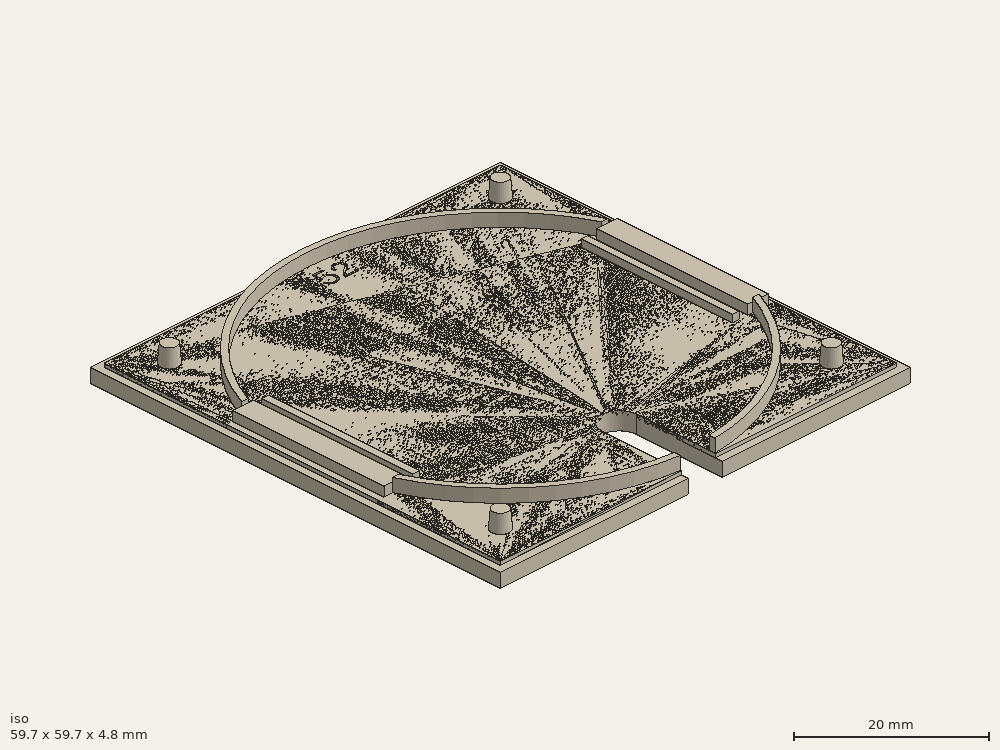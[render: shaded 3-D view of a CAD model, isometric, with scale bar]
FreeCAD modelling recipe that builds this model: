
FCSTD DOCUMENT  (FreeCAD 0.16R)
Label: edizio_part_752_cable-slot
License: All rights reserved
LicenseURL: http://en.wikipedia.org/wiki/All_rights_reserved
objects: Part::Box×25, Part::Cut×9, Part::Cone×4, Part::Cylinder×3, Part::Fuse×2, Part::Part2DObjectPython×1, Part::Extrusion×1, Part::FeaturePython×1
note: 46 computed .brp shape members not serialized (recipe doc carries the construction recipe); baked Part::Feature solids carry a one-line shape summary decoded from their .brp

FEATURE [Part::Box] Box  label="Front"
  Height = 1.9
  Length = 59.7
  Width = 59.7
FEATURE [Part::Box] Box001  label="Layer_Inside_Base"
  Height = 0.5
  Length = 57.7
  Placement = pos=(1,1,1.9) rot=(0,0,1;0rad)
  Width = 57.7
FEATURE [Part::Cylinder] Cylinder  label="Cylinder_Outside"
  Angle = 360
  Height = 1.8
  Placement = pos=(29.85,29.85,2.4) rot=(0,0,1;0rad)
  Radius = 28.85
FEATURE [Part::Cylinder] Cylinder001  label="Cylinder_Inside"
  Angle = 360
  Height = 1.8
  Placement = pos=(29.85,29.85,2.4) rot=(0,0,1;0rad)
  Radius = 28
FEATURE [Part::Cut] Cut  label="Cylinder_Base"
  Base = -> Cylinder
  Tool = -> Cylinder001
FEATURE [Part::Cone] Cone  label="Cone_001"
  Angle = 360
  Height = 2.4
  Placement = pos=(5.8,5.8,2.4) rot=(0,0,1;0rad)
  Radius1 = 1.25
  Radius2 = 1.05
FEATURE [Part::Cone] Cone001  label="Cone_002"
  Angle = 360
  Height = 2.4
  Placement = pos=(54,5.8,2.4) rot=(0,0,1;0rad)
  Radius1 = 1.25
  Radius2 = 1.05
FEATURE [Part::Cone] Cone002  label="Cone_003"
  Angle = 360
  Height = 2.4
  Placement = pos=(54,54,2.4) rot=(0,0,1;0rad)
  Radius1 = 1.25
  Radius2 = 1.05
FEATURE [Part::Cone] Cone003  label="Cone_004"
  Angle = 360
  Height = 2.4
  Placement = pos=(5.8,54,2.4) rot=(0,0,1;0rad)
  Radius1 = 1.25
  Radius2 = 1.05
FEATURE [Part::Box] Box002  label="Cut_001"
  Height = 2.5
  Length = 5
  Placement = pos=(0,18.85,1.9) rot=(0,0,1;0rad)
  Width = 22
FEATURE [Part::Box] Box003  label="Cut_002"
  Height = 2.5
  Length = 5
  Placement = pos=(54.7,18.85,1.9) rot=(0,0,1;0rad)
  Width = 22
FEATURE [Part::Cut] Cut001  label="Cylinder_Cut001"
  Base = -> Cut
  Tool = -> Box002
FEATURE [Part::Cut] Cut002  label="Cylinder"
  Base = -> Cut001
  Tool = -> Box003
FEATURE [Part::Box] Box004  label="Cut_003"
  Height = 1.9
  Length = 5
  Placement = pos=(0,18.85,1.9) rot=(0,0,1;0rad)
  Width = 22
FEATURE [Part::Box] Box005  label="Cut_004"
  Height = 1.9
  Length = 5
  Placement = pos=(54.7,18.85,1.9) rot=(0,0,1;0rad)
  Width = 22
FEATURE [Part::Cut] Cut003  label="Layer_Inside_Cut003"
  Base = -> Box001
  Tool = -> Box004
FEATURE [Part::Cut] Cut004  label="Layer_Inside"
  Base = -> Cut003
  Tool = -> Box005
FEATURE [Part::Box] Box006  label="Cube_001"
  Height = 0.1
  Length = 1
  Placement = pos=(1.9,21,1.9) rot=(0,0,1;0rad)
  Width = 1
FEATURE [Part::Box] Box007  label="Cube_002"
  Height = 0.1
  Length = 1
  Placement = pos=(1.9,27.7,1.9) rot=(0,0,1;0rad)
  Width = 1
FEATURE [Part::Box] Box008  label="Cube_003"
  Height = 0.1
  Length = 1
  Placement = pos=(1.9,30.9,1.9) rot=(0,0,1;0rad)
  Width = 1
FEATURE [Part::Box] Box009  label="Cube_004"
  Height = 0.1
  Length = 1
  Placement = pos=(1.9,37.7,1.9) rot=(0,0,1;0rad)
  Width = 1
FEATURE [Part::Box] Box010  label="Cube_005"
  Height = 0.1
  Length = 1
  Placement = pos=(56.8,21,1.9) rot=(0,0,1;0rad)
  Width = 1
FEATURE [Part::Box] Box011  label="Cube_006"
  Height = 0.1
  Length = 1
  Placement = pos=(56.8,27.7,1.9) rot=(0,0,1;0rad)
  Width = 1
FEATURE [Part::Box] Box012  label="Cube_007"
  Height = 0.1
  Length = 1
  Placement = pos=(56.8,30.9,1.9) rot=(0,0,1;0rad)
  Width = 1
FEATURE [Part::Box] Box013  label="Cube_008"
  Height = 0.1
  Length = 1
  Placement = pos=(56.8,37.7,1.9) rot=(0,0,1;0rad)
  Width = 1
FEATURE [Part::Box] Box014  label="Cube_011"
  Height = 0.4
  Length = 3
  Placement = pos=(1.9,18.85,1.9) rot=(0,0,1;0rad)
  Width = 1.3
FEATURE [Part::Box] Box015  label="Cube_012"
  Height = 0.4
  Length = 3
  Placement = pos=(54.9,18.85,1.9) rot=(0,0,1;0rad)
  Width = 1.3
FEATURE [Part::Box] Box016  label="Cube_013"
  Height = 0.4
  Length = 3
  Placement = pos=(1.9,39.55,1.9) rot=(0,0,1;0rad)
  Width = 1.3
FEATURE [Part::Box] Box017  label="Cube_014"
  Height = 0.4
  Length = 3
  Placement = pos=(54.9,39.55,1.9) rot=(0,0,1;0rad)
  Width = 1.3
FEATURE [Part::Box] Box018  label="Cube_015"
  Height = 0.4
  Length = 3
  Placement = pos=(1.9,29.35,1.9) rot=(0,0,1;0rad)
  Width = 1
FEATURE [Part::Box] Box019  label="Cube_016"
  Height = 0.4
  Length = 3
  Placement = pos=(54.9,29.35,1.9) rot=(0,0,1;0rad)
  Width = 1
FEATURE [Part::Box] Box020  label="Cube_021"
  Height = 1.4
  Length = 3
  Placement = pos=(1.9,18.85,2.3) rot=(0,0,1;0rad)
  Width = 22
FEATURE [Part::Box] Box021  label="Cube_022"
  Height = 1.4
  Length = 3
  Placement = pos=(54.86,18.85,2.3) rot=(0,0,1;0rad)
  Width = 22
FEATURE [Part::Box] Box022  label="Cube_031"
  Height = 1
  Length = 1
  Placement = pos=(6.1,18.85,2.4) rot=(0,0,1;0rad)
  Width = 22
FEATURE [Part::Box] Box023  label="Cube_032"
  Height = 1
  Length = 1
  Placement = pos=(52.6,18.85,2.4) rot=(0,0,1;0rad)
  Width = 22
FEATURE [Part::Part2DObjectPython] ShapeString  # Draft 2D object (typed FeaturePython)
  FontFile = <path>
  Size = 0.1
  String = 752
  Tracking = 0
FEATURE [Part::Extrusion] Extrude001
  Base = -> ShapeString
  Dir = (0,0,0.1)
  Placement = pos=(0,0,1.9) rot=(0,0,1;0rad)
  Solid = true
FEATURE [Part::FeaturePython] Scale  # Draft clone (typed FeaturePython)
  Objects = -> [Extrude001]
  Placement = pos=(25.9,53.5,4.4) rot=(0,0,1;0rad)
  Scale = (22,22,0)
FEATURE [Part::Cylinder] Cylinder002  label="Cylinder001"
  Angle = 360
  Height = 5
  Placement = pos=(29.85,12.5,0) rot=(0,0,1;0rad)
  Radius = 2.5
FEATURE [Part::Box] Box024  label="Cube"
  Height = 5
  Length = 5
  Placement = pos=(27.35,0,0) rot=(0,0,1;0rad)
  Width = 12.5
FEATURE [Part::Fuse] Fusion  label="Plate"
  Base = -> Box
  Tool = -> Box001
FEATURE [Part::Fuse] Fusion001  label="Plate_and_Ring"
  Base = -> Cut002
  Tool = -> Fusion
FEATURE [Part::Cut] Cut005
  Base = -> Fusion001
  Tool = -> Box024
FEATURE [Part::Cut] Cut006
  Base = -> Cut005
  Tool = -> Cylinder002
FEATURE [Part::Cut] Cut007
  Base = -> Cut004
  Tool = -> Cylinder002
FEATURE [Part::Cut] Cut008
  Base = -> Cut007
  Tool = -> Box024
note: 1 file-system path scrubbed to <path> (originals preserved in the JSON sidecar)
